# Revit family: AV5030001_Grifería para Lavaplatos sencilloAluvia Palanca
name_source: partatom
category: Plumbing Fixtures
units: mm (PartAtom-declared; Revit-internal decimal feet)

## family parameters
Cut with Voids When Loaded = No
Host = Face
OmniClass Number = 23.21.23.23
OmniClass Title = Residential Food Cooking Equipment
Part Type = Normal
Room Calculation Point = No
Round Connector Dimension = Use Diameter
Shared = No

## types (1)
- AV5030001_Grifería para Lavaplatos sencilloAluvia Palanca
    Acabado = Corona_Plastico_Cromado
    Creado por = IDD
    Default Elevation = 900 mm  [stored 2.95276 ft]
    Depth = 198 mm  [stored 0.649606 ft]
    Description = La grifería de cocina Aluvia ha sido diseñada para trabajar en perfecta armonía con el espacio. Su pico giratorio le permite al usuario tomar ventaja de toda el área de la poceta. Pico alto que permite el lavado de elementos de gran tamaño, dando confortnen el uso.
    Fecha de creación = 30/09/2020
    Height = 336 mm  [stored 1.10236 ft]
    Manufacturer = Corona
    Material = Corona_Plastico_Cromado
    Maximum gauge working pressure of water = 125 psi (862 Kpa).
    Model = Griferia LavaPlatos Aluvia 8 Pulgadas Triceta
    Pick Life or Wear (Rotary) = 50.000 ciclos.
    Recommended minimum pressure = 20 psi (138 Kpa).
    Reference = AV5030001
    SKU = AV5030001
    Service life or wear (unit) = 500.000 ciclos.
    URL = https://corona.co
    Warranty = 30  Años Grival - 2 Años Cromado
    Width = 260 mm  [stored 0.853018 ft]

note: [stored X ft] marks values corroborated as IEEE doubles in the binary element streams (Revit-internal decimal feet)

## geometry (parser evidence)
native form markers: Sweep x4
no freeform markers — native parametric forms only
